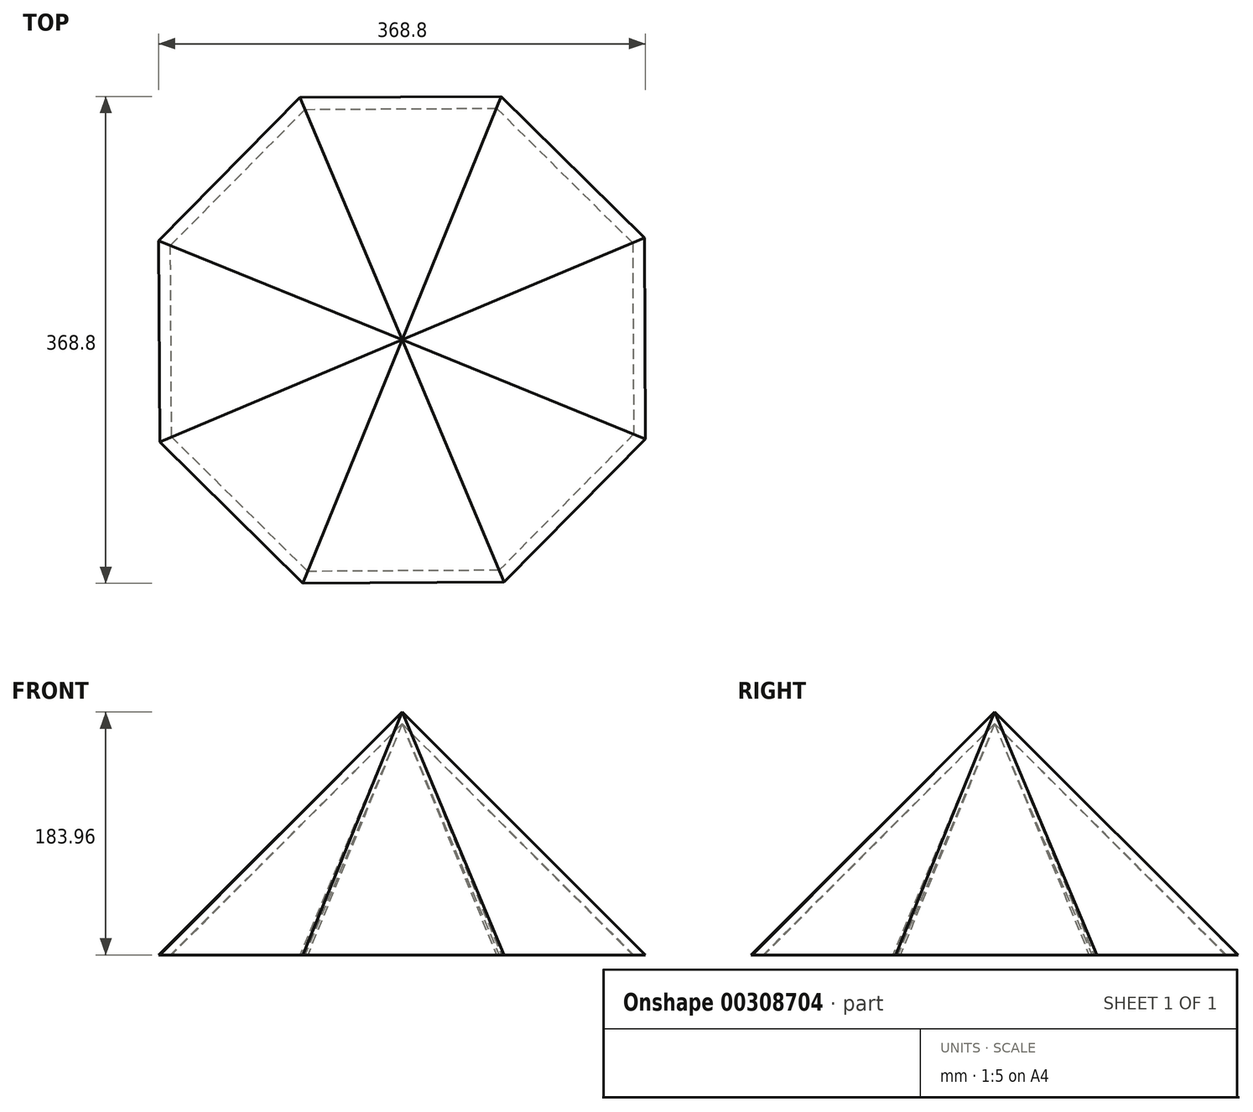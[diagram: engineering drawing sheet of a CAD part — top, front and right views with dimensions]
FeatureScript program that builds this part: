
annotation { "Feature Type Name" : "Feature", "Feature Type Description" : "" }
export const myFeature = defineFeature(function(context is Context, id is Id, definition is map)
    precondition{}
    {
        {
            var Q0;
            Q0=qCreatedBy(makeId("Top.planeOp"),FACE);
            var sketch = newSketch(context, id + "F0", { "sketchPlane" : qUnion([Q0])});
            skCircle(sketch, "E0.cCircle", {"center": v(0, 0) * mm, "radius": 183.96 * mm, "construction": true});
            skLineSegment(sketch, "E0.0", {"start": v(-184.4, 75.14) * mm, "end": v(-77.26, 183.52) * mm});
            skLineSegment(sketch, "E0.1", {"start": v(-77.26, 183.52) * mm, "end": v(75.14, 184.4) * mm});
            skLineSegment(sketch, "E0.2", {"start": v(75.14, 184.4) * mm, "end": v(183.52, 77.26) * mm});
            skLineSegment(sketch, "E0.3", {"start": v(183.52, 77.26) * mm, "end": v(184.4, -75.14) * mm});
            skLineSegment(sketch, "E0.4", {"start": v(184.4, -75.14) * mm, "end": v(77.26, -183.52) * mm});
            skLineSegment(sketch, "E0.5", {"start": v(77.26, -183.52) * mm, "end": v(-75.14, -184.4) * mm});
            skLineSegment(sketch, "E0.6", {"start": v(-75.14, -184.4) * mm, "end": v(-183.52, -77.26) * mm});
            skLineSegment(sketch, "E0.7", {"start": v(-183.52, -77.26) * mm, "end": v(-184.4, 75.14) * mm});
            skPoint(sketch, "E0.0.midPoint", {"position": v(-130.83, 129.33) * mm});
            skSolve(sketch);
        }
        {
            var Q0;
            Q0=makeQuery(id+"F0.imprint","IMPRINT",FACE,{"disambiguationData":[TD([[makeQuery(id+"F0.imprint","IMPRINT",EDGE,{"derivedFrom":sQuery(id+"F0.wireOp",EDGE,"E0.0")}),-1.0]])]});
            extrude(context, id + "F1", {"entities" : qUnion([Q0]), "depth" : 184.15 * mm, "hasDraft" : true, "draftAngle" : 45 * degree, "draftPullDirection" : true});
        }
        {
            var Q0;
            Q0=makeQuery(id+"F1.opExtrude","CAP_FACE",FACE,{"disambiguationData":[OSD([sQuery(id+"F0.wireOp",EDGE,"E0.0"),sQuery(id+"F0.wireOp",EDGE,"E0.1"),sQuery(id+"F0.wireOp",EDGE,"E0.2"),sQuery(id+"F0.wireOp",EDGE,"E0.3"),sQuery(id+"F0.wireOp",EDGE,"E0.4"),sQuery(id+"F0.wireOp",EDGE,"E0.5"),sQuery(id+"F0.wireOp",EDGE,"E0.6"),sQuery(id+"F0.wireOp",EDGE,"E0.7")])],"isStart":true});
            shell(context, id + "F2", {"entities" : qUnion([Q0]), "thickness" : 6.35 * mm});
        }
    });
